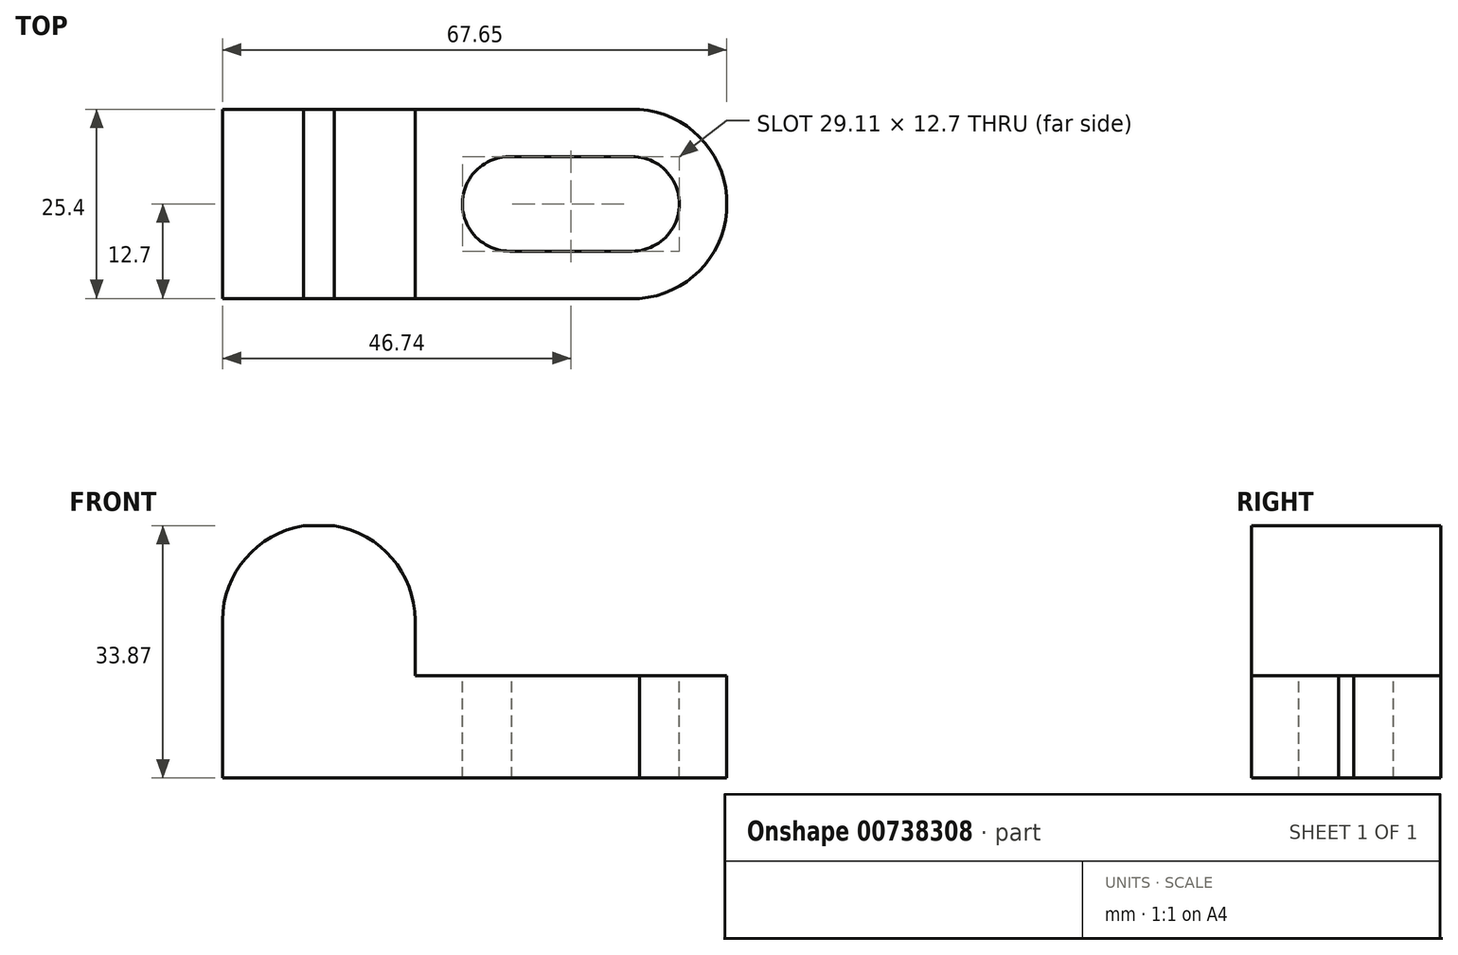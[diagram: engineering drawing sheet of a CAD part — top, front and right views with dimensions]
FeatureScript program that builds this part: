
annotation { "Feature Type Name" : "Feature", "Feature Type Description" : "" }
export const myFeature = defineFeature(function(context is Context, id is Id, definition is map)
    precondition{}
    {
        {
            var Q0;
            Q0=qCreatedBy(makeId("Front.planeOp"),FACE);
            var sketch = newSketch(context, id + "F0", { "sketchPlane" : qUnion([Q0])});
            skLineSegment(sketch, "E0", {"start": v(0, 0) * mm, "end": v(0, 33.87) * mm});
            skLineSegment(sketch, "E1", {"start": v(0, 33.87) * mm, "end": v(25.83, 33.87) * mm});
            skLineSegment(sketch, "E2", {"start": v(25.83, 33.87) * mm, "end": v(25.83, 13.77) * mm});
            skLineSegment(sketch, "E3", {"start": v(25.83, 13.77) * mm, "end": v(67.65, 13.77) * mm});
            skLineSegment(sketch, "E4", {"start": v(67.65, 13.77) * mm, "end": v(67.65, 0) * mm});
            skLineSegment(sketch, "E5", {"start": v(67.65, 0) * mm, "end": v(0, 0) * mm});
            skSolve(sketch);
        }
        {
            var Q0;
            Q0=makeQuery(id+"F0.imprint","IMPRINT",FACE,{"disambiguationData":[TD([[makeQuery(id+"F0.imprint","IMPRINT",EDGE,{"derivedFrom":sQuery(id+"F0.wireOp",EDGE,"E0")}),-1.0]])]});
            extrude(context, id + "F1", {"entities" : qUnion([Q0]), "depth" : 25.4 * mm, "offsetDistance" : 25.4 * mm});
        }
        {
            var Q0;
            Q0=makeQuery(id+"F1.opExtrude","CAP_FACE",FACE,{"disambiguationData":[OSD([sQuery(id+"F0.wireOp",EDGE,"E0"),sQuery(id+"F0.wireOp",EDGE,"E1"),sQuery(id+"F0.wireOp",EDGE,"E2"),sQuery(id+"F0.wireOp",EDGE,"E3"),sQuery(id+"F0.wireOp",EDGE,"E4"),sQuery(id+"F0.wireOp",EDGE,"E5")])],"isStart":false});
            var sketch = newSketch(context, id + "F2", { "sketchPlane" : qUnion([Q0])});
            skLineSegment(sketch, "E6", {"start": v(0, 21.17) * mm, "end": v(12.7, 21.17) * mm});
            skCircle(sketch, "E7", {"center": v(12.7, 21.17) * mm, "radius": 6.35 * mm});
            skLineSegment(sketch, "E8", {"start": v(0, 21.17) * mm, "end": v(25.83, 21.17) * mm});
            skArc(sketch, "E9", {"start": v(25.83, 21.17) * mm, "mid": v(12.92, 34.04) * mm, "end": v(0, 21.17) * mm});
            skSolve(sketch);
        }
        {
            var Q0;
            {var subQ1=makeQuery(id+"F1.opExtrude","CAP_EDGE",EDGE,{"disambiguationData":[OSD([sQuery(id+"F0.wireOp",EDGE,"E0")])],"isStart":false});var subQ3=makeQuery(id+"F1.opExtrude","CAP_EDGE",EDGE,{"disambiguationData":[OSD([sQuery(id+"F0.wireOp",EDGE,"E1")])],"isStart":false});var subQ5=makeQuery(id+"F2.imprint","INTERSECT",VERTEX,{"derivedFrom":[subQ1,subQ3]});Q0=makeQuery(id+"F2.imprint","IMPRINT",FACE,{"disambiguationData":[TD([[makeQuery(id+"F2.imprint","IMPRINT",EDGE,{"disambiguationData":[TD([[subQ5,-1.0]])],"derivedFrom":subQ3}),-1.0]])]});}
            var Q1;
            {var subQ1=makeQuery(id+"F1.opExtrude","CAP_EDGE",EDGE,{"disambiguationData":[OSD([sQuery(id+"F0.wireOp",EDGE,"E2")])],"isStart":false});var subQ3=makeQuery(id+"F1.opExtrude","CAP_EDGE",EDGE,{"disambiguationData":[OSD([sQuery(id+"F0.wireOp",EDGE,"E1")])],"isStart":false});var subQ5=makeQuery(id+"F2.imprint","INTERSECT",VERTEX,{"derivedFrom":[subQ3,subQ1]});Q1=makeQuery(id+"F2.imprint","IMPRINT",FACE,{"disambiguationData":[TD([[makeQuery(id+"F2.imprint","IMPRINT",EDGE,{"disambiguationData":[TD([[subQ5,1.0]])],"derivedFrom":subQ3}),-1.0]])]});}
            var Q2;
            {var subQ0=sQuery(id+"F2.wireOp",EDGE,"E8");var subQ4=makeQuery(id+"F2.imprint","IMPRINT",VERTEX,{"derivedFrom":subQ0});Q2=makeQuery(id+"F2.imprint","IMPRINT",FACE,{"disambiguationData":[TD([[makeQuery(id+"F2.imprint","IMPRINT",EDGE,{"disambiguationData":[TD([[subQ4,1.0]])],"derivedFrom":subQ0}),1.0]])]});}
            var Q3;
            {var subQ0=sQuery(id+"F2.wireOp",EDGE,"E8");var subQ4=makeQuery(id+"F2.imprint","IMPRINT",VERTEX,{"derivedFrom":subQ0});Q3=makeQuery(id+"F2.imprint","IMPRINT",FACE,{"disambiguationData":[TD([[makeQuery(id+"F2.imprint","IMPRINT",EDGE,{"disambiguationData":[TD([[subQ4,1.0]])],"derivedFrom":subQ0}),-1.0]])]});}
            extrude(context, id + "F3", {"entities" : qUnion([Q0, Q1, Q2, Q3]), "operationType" : NewBodyOperationType.REMOVE, "oppositeDirection" : true, "depth" : 50.8 * mm, "offsetDistance" : 25.4 * mm});
        }
        {
            var Q0;
            Q0=makeQuery(id+"F1.opExtrude","SWEPT_FACE",FACE,{"disambiguationData":[OSD([sQuery(id+"F0.wireOp",EDGE,"E3")])]});
            var sketch = newSketch(context, id + "F4", { "sketchPlane" : qUnion([Q0])});
            skCircle(sketch, "E10", {"center": v(38.53, -12.7) * mm, "radius": 6.35 * mm});
            skCircle(sketch, "E11", {"center": v(54.95, -12.7) * mm, "radius": 6.35 * mm});
            skSolve(sketch);
        }
        {
            var Q0;
            Q0=makeQuery(id+"F4.imprint","IMPRINT",FACE,{"disambiguationData":[TD([[makeQuery(id+"F4.imprint","IMPRINT",EDGE,{"derivedFrom":sQuery(id+"F4.wireOp",EDGE,"E10")}),1.0]])]});
            var Q1;
            Q1=makeQuery(id+"F4.imprint","IMPRINT",FACE,{"disambiguationData":[TD([[makeQuery(id+"F4.imprint","IMPRINT",EDGE,{"derivedFrom":sQuery(id+"F4.wireOp",EDGE,"E11")}),1.0]])]});
            extrude(context, id + "F5", {"entities" : qUnion([Q0, Q1]), "operationType" : NewBodyOperationType.REMOVE, "endBound" : BoundingType.THROUGH_ALL, "oppositeDirection" : true, "depth" : 25.4 * mm, "offsetDistance" : 25.4 * mm});
        }
        {
            var Q0;
            Q0=makeQuery(id+"F1.opExtrude","SWEPT_FACE",FACE,{"disambiguationData":[OSD([sQuery(id+"F0.wireOp",EDGE,"E3")])]});
            var sketch = newSketch(context, id + "F6", { "sketchPlane" : qUnion([Q0])});
            skLineSegment(sketch, "E12", {"start": v(38.82, -6.36) * mm, "end": v(54.94, -6.35) * mm});
            skLineSegment(sketch, "E13", {"start": v(54.94, -19.05) * mm, "end": v(38.53, -19.05) * mm});
            skSolve(sketch);
        }
        {
            var Q0;
            {var subQ0=sQuery(id+"F6.wireOp",EDGE,"E12");Q0=makeQuery(id+"F6.imprint","IMPRINT",FACE,{"disambiguationData":[TD([[makeQuery(id+"F6.imprint","IMPRINT",EDGE,{"derivedFrom":subQ0}),-1.0]])]});}
            extrude(context, id + "F7", {"entities" : qUnion([Q0]), "operationType" : NewBodyOperationType.REMOVE, "endBound" : BoundingType.THROUGH_ALL, "oppositeDirection" : true, "depth" : 25.4 * mm, "offsetDistance" : 25.4 * mm});
        }
        {
            var Q0;
            Q0=makeQuery(id+"F1.opExtrude","SWEPT_FACE",FACE,{"disambiguationData":[OSD([sQuery(id+"F0.wireOp",EDGE,"E3")])]});
            var sketch = newSketch(context, id + "F8", { "sketchPlane" : qUnion([Q0])});
            skCircle(sketch, "E14", {"center": v(54.95, -12.7) * mm, "radius": 12.74 * mm});
            skSolve(sketch);
        }
        {
            var Q0;
            {var subQ0=sQuery(id+"F8.wireOp",EDGE,"E14");var subQ1=sQuery(id+"F0.wireOp",EDGE,"E3");var subQ2=makeQuery(id+"F1.opExtrude","CAP_EDGE",EDGE,{"disambiguationData":[OSD([subQ1])],"isStart":true});var subQ3=makeQuery(id+"F8.imprint","INTERSECT",VERTEX,{"disambiguationData":[OD(0.0)],"derivedFrom":[subQ2,subQ0]});Q0=makeQuery(id+"F8.imprint","IMPRINT",FACE,{"disambiguationData":[TD([[makeQuery(id+"F8.imprint","IMPRINT",EDGE,{"disambiguationData":[TD([[subQ3,1.0]])],"derivedFrom":subQ0}),-1.0]])]});}
            var Q1;
            {var subQ0=sQuery(id+"F8.wireOp",EDGE,"E14");var subQ1=sQuery(id+"F0.wireOp",EDGE,"E3");var subQ2=makeQuery(id+"F1.opExtrude","CAP_EDGE",EDGE,{"disambiguationData":[OSD([subQ1])],"isStart":false});var subQ3=makeQuery(id+"F8.imprint","INTERSECT",VERTEX,{"disambiguationData":[OD(1.0)],"derivedFrom":[subQ2,subQ0]});Q1=makeQuery(id+"F8.imprint","IMPRINT",FACE,{"disambiguationData":[TD([[makeQuery(id+"F8.imprint","IMPRINT",EDGE,{"disambiguationData":[TD([[subQ3,-1.0]])],"derivedFrom":subQ0}),-1.0]])]});}
            extrude(context, id + "F9", {"entities" : qUnion([Q0, Q1]), "operationType" : NewBodyOperationType.REMOVE, "endBound" : BoundingType.THROUGH_ALL, "oppositeDirection" : true, "depth" : 25.4 * mm, "offsetDistance" : 25.4 * mm});
        }
    });
